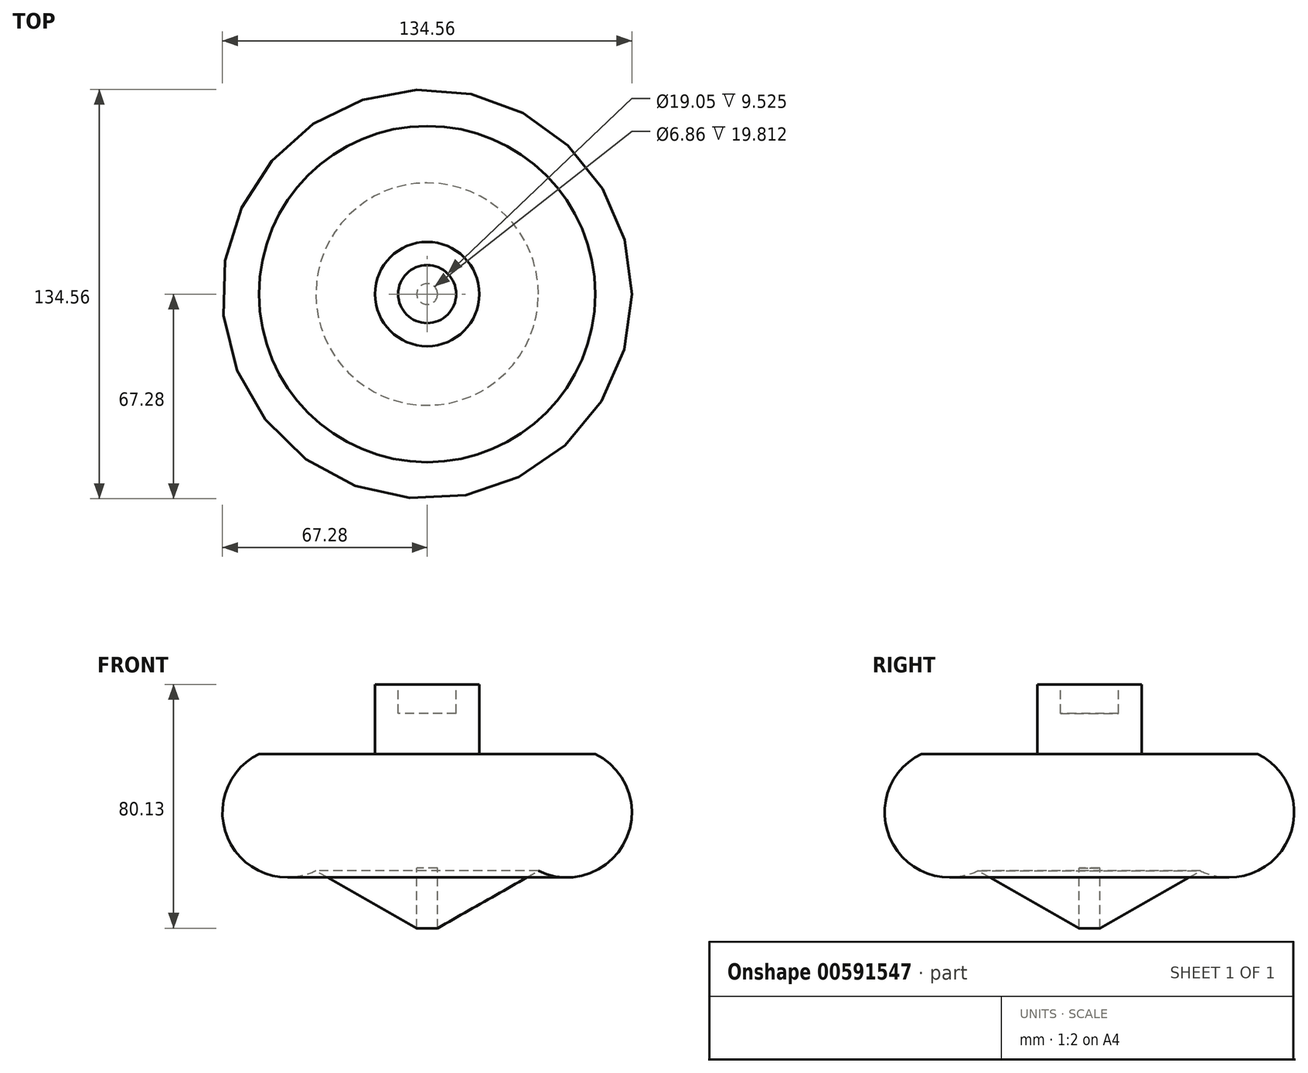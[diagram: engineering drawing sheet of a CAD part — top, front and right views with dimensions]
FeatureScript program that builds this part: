
annotation { "Feature Type Name" : "Feature", "Feature Type Description" : "" }
export const myFeature = defineFeature(function(context is Context, id is Id, definition is map)
    precondition{}
    {
        {
            var Q0;
            Q0=qCreatedBy(makeId("Front.planeOp"),FACE);
            var sketch = newSketch(context, id + "F0", { "sketchPlane" : qUnion([Q0])});
            skLineSegment(sketch, "E0", {"start": v(55.24, 58.67) * mm, "end": v(17.14, 58.67) * mm});
            skLineSegment(sketch, "E1", {"start": v(17.14, 58.67) * mm, "end": v(17.14, 81.53) * mm});
            skLineSegment(sketch, "E2", {"start": v(17.14, 81.53) * mm, "end": v(9.52, 81.53) * mm});
            skLineSegment(sketch, "E3", {"start": v(9.52, 81.53) * mm, "end": v(9.52, 72) * mm});
            skLineSegment(sketch, "E4", {"start": v(9.52, 72) * mm, "end": v(0, 72) * mm});
            skLineSegment(sketch, "E5", {"start": v(0, 72) * mm, "end": v(0, 21.2) * mm});
            skLineSegment(sketch, "E6", {"start": v(0, 21.2) * mm, "end": v(3.43, 21.2) * mm});
            skLineSegment(sketch, "E7", {"start": v(3.43, 21.2) * mm, "end": v(3.43, 1.4) * mm});
            skLineSegment(sketch, "E8", {"start": v(3.43, 1.4) * mm, "end": v(36.55, 20.22) * mm});
            skArc(sketch, "E9", {"start": v(36.55, 20.22) * mm, "mid": v(65.13, 30.1) * mm, "end": v(55.24, 58.67) * mm});
            skSolve(sketch);
        }
        {
            var Q0;
            Q0=makeQuery(id+"F0.imprint","IMPRINT",FACE,{"disambiguationData":[TD([[makeQuery(id+"F0.imprint","IMPRINT",EDGE,{"derivedFrom":sQuery(id+"F0.wireOp",EDGE,"E0")}),1.0]])]});
            var Q1;
            Q1=sQuery(id+"F0.wireOp",EDGE,"E5");
            revolve(context, id + "F1", {"entities" : qUnion([Q0]), "axis" : qUnion([Q1]), "revolveType" : RevolveType.FULL});
        }
    });
